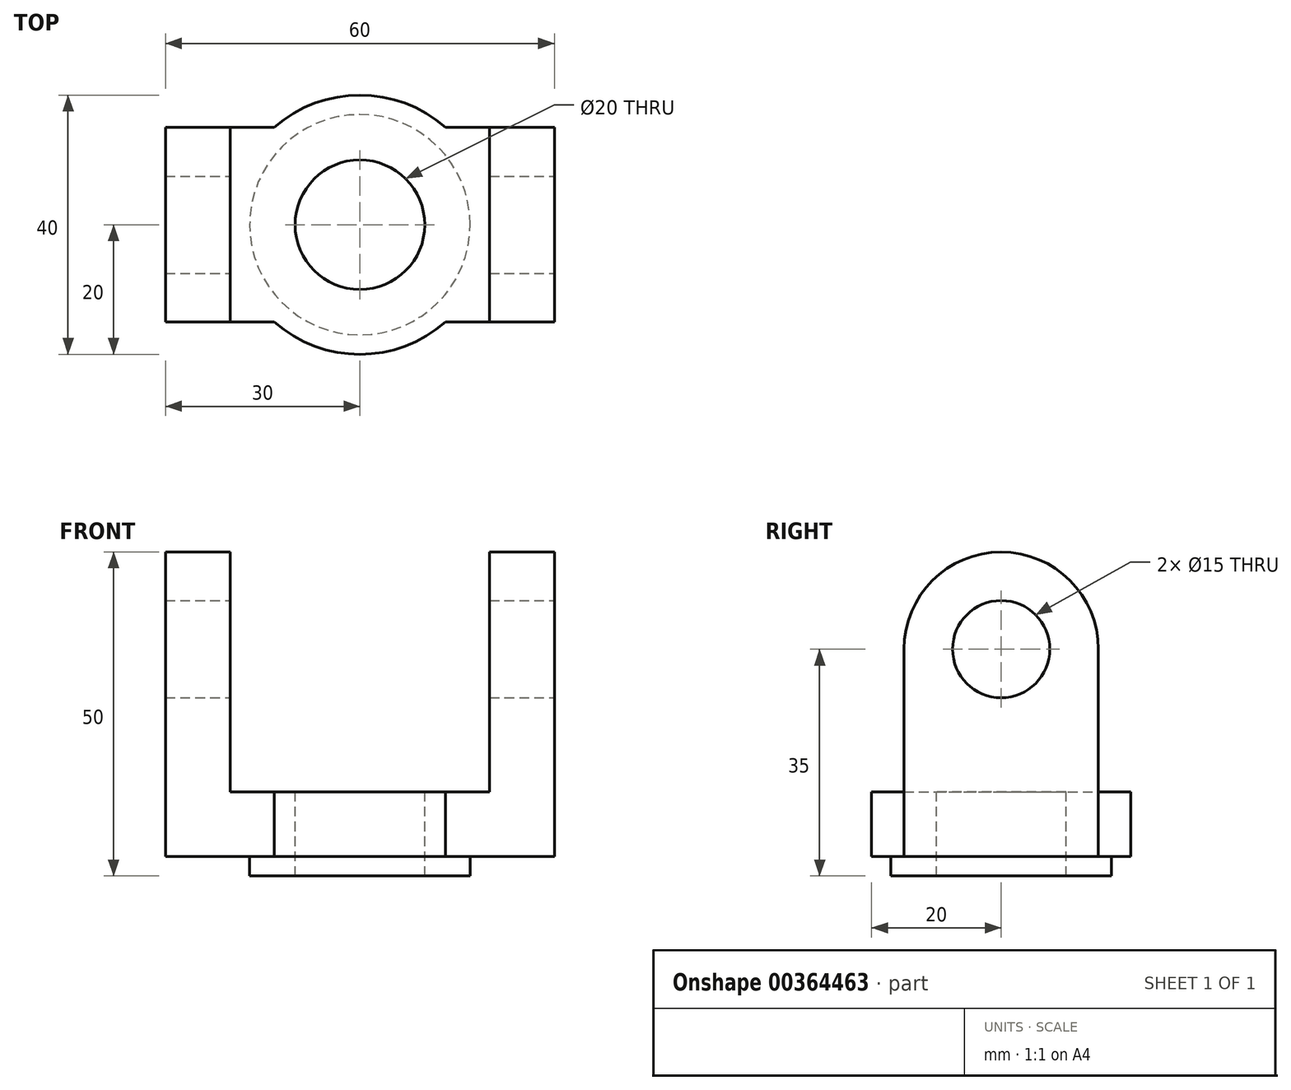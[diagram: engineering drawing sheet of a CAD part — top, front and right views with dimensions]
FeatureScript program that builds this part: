
annotation { "Feature Type Name" : "Feature", "Feature Type Description" : "" }
export const myFeature = defineFeature(function(context is Context, id is Id, definition is map)
    precondition{}
    {
        {
            var Q0;
            Q0=qCreatedBy(makeId("Top.planeOp"),FACE);
            var sketch = newSketch(context, id + "F0", { "sketchPlane" : qUnion([Q0])});
            skCircle(sketch, "E0", {"center": v(0, 0) * mm, "radius": 17 * mm});
            skSolve(sketch);
        }
        {
            var Q0;
            Q0 = qSketchRegion(id + "F0", true);
            extrude(context, id + "F1", {"entities" : qUnion([Q0]), "depth" : 3 * mm});
        }
        {
            var Q0;
            Q0=makeQuery(id+"F1.opExtrude","CAP_FACE",FACE,{"disambiguationData":[OSD([sQuery(id+"F0.wireOp",EDGE,"E0")])],"isStart":false});
            var sketch = newSketch(context, id + "F2", { "sketchPlane" : qUnion([Q0])});
            skCircle(sketch, "E1", {"center": v(0, 0) * mm, "radius": 20 * mm});
            skLineSegment(sketch, "E2.bottom", {"start": v(-30, -15) * mm, "end": v(30, -15) * mm});
            skLineSegment(sketch, "E2.top", {"start": v(-30, 15) * mm, "end": v(30, 15) * mm});
            skLineSegment(sketch, "E2.left", {"start": v(-30, -15) * mm, "end": v(-30, 15) * mm});
            skLineSegment(sketch, "E2.right", {"start": v(30, -15) * mm, "end": v(30, 15) * mm});
            skSolve(sketch);
        }
        {
            var Q0;
            Q0 = qSketchRegion(id + "F2", true);
            extrude(context, id + "F3", {"entities" : qUnion([Q0]), "operationType" : NewBodyOperationType.ADD, "depth" : 10 * mm});
        }
        {
            var Q0;
            Q0=makeQuery(id+"F3.opExtrude","CAP_FACE",FACE,{"disambiguationData":[OSD([sQuery(id+"F2.wireOp",EDGE,"E1"),sQuery(id+"F2.wireOp",EDGE,"E2.bottom"),sQuery(id+"F2.wireOp",EDGE,"E2.top"),sQuery(id+"F2.wireOp",EDGE,"E2.left"),sQuery(id+"F2.wireOp",EDGE,"E2.right")])],"isStart":false});
            var sketch = newSketch(context, id + "F4", { "sketchPlane" : qUnion([Q0])});
            skCircle(sketch, "E3", {"center": v(0, 0) * mm, "radius": 10 * mm});
            skSolve(sketch);
        }
        {
            var Q0;
            Q0 = qSketchRegion(id + "F4", true);
            extrude(context, id + "F5", {"entities" : qUnion([Q0]), "operationType" : NewBodyOperationType.REMOVE, "endBound" : BoundingType.THROUGH_ALL, "oppositeDirection" : true, "depth" : 25 * mm});
        }
        {
            var Q0;
            Q0=makeQuery(id+"F3.opExtrude","CAP_FACE",FACE,{"disambiguationData":[OSD([sQuery(id+"F2.wireOp",EDGE,"E1"),sQuery(id+"F2.wireOp",EDGE,"E2.bottom"),sQuery(id+"F2.wireOp",EDGE,"E2.top"),sQuery(id+"F2.wireOp",EDGE,"E2.left"),sQuery(id+"F2.wireOp",EDGE,"E2.right")])],"isStart":false});
            var sketch = newSketch(context, id + "F6", { "sketchPlane" : qUnion([Q0])});
            skLineSegment(sketch, "E4.bottom", {"start": v(-30, -15) * mm, "end": v(-20, -15) * mm});
            skLineSegment(sketch, "E4.top", {"start": v(-30, 15) * mm, "end": v(-20, 15) * mm});
            skLineSegment(sketch, "E4.left", {"start": v(-30, -15) * mm, "end": v(-30, 15) * mm});
            skLineSegment(sketch, "E4.right", {"start": v(-20, -15) * mm, "end": v(-20, 15) * mm});
            skLineSegment(sketch, "E5.bottom", {"start": v(30, -15) * mm, "end": v(20, -15) * mm});
            skLineSegment(sketch, "E5.top", {"start": v(30, 15) * mm, "end": v(20, 15) * mm});
            skLineSegment(sketch, "E5.left", {"start": v(30, -15) * mm, "end": v(30, 15) * mm});
            skLineSegment(sketch, "E5.right", {"start": v(20, -15) * mm, "end": v(20, 15) * mm});
            skSolve(sketch);
        }
        {
            var Q0;
            Q0 = qSketchRegion(id + "F6", true);
            extrude(context, id + "F7", {"entities" : qUnion([Q0]), "operationType" : NewBodyOperationType.ADD, "depth" : 40 * mm});
        }
        {
            var Q0;
            Q0=makeQuery(id+"F7.boolean.opBoolean","MERGE",FACE,{"derivedFrom":[makeQuery(id+"F3.opExtrude","SWEPT_FACE",FACE,{"disambiguationData":[OSD([sQuery(id+"F2.wireOp",EDGE,"E2.right")])]}),makeQuery(id+"F7.opExtrude","SWEPT_FACE",FACE,{"disambiguationData":[OSD([sQuery(id+"F6.wireOp",EDGE,"E5.left")])]})]});
            var sketch = newSketch(context, id + "F8", { "sketchPlane" : qUnion([Q0])});
            skCircle(sketch, "E6", {"center": v(0, 35) * mm, "radius": 7.5 * mm});
            skSolve(sketch);
        }
        {
            var Q0;
            Q0 = qSketchRegion(id + "F8", true);
            extrude(context, id + "F9", {"entities" : qUnion([Q0]), "operationType" : NewBodyOperationType.REMOVE, "endBound" : BoundingType.THROUGH_ALL, "oppositeDirection" : true, "depth" : 25 * mm});
        }
        {
            var Q0;
            Q0=makeQuery(id+"F7.boolean.opBoolean","MERGE",FACE,{"derivedFrom":[makeQuery(id+"F3.opExtrude","SWEPT_FACE",FACE,{"disambiguationData":[OSD([sQuery(id+"F2.wireOp",EDGE,"E2.right")])]}),makeQuery(id+"F7.opExtrude","SWEPT_FACE",FACE,{"disambiguationData":[OSD([sQuery(id+"F6.wireOp",EDGE,"E5.left")])]})]});
            var sketch = newSketch(context, id + "F10", { "sketchPlane" : qUnion([Q0])});
            skArc(sketch, "E7", {"start": v(15, 35) * mm, "mid": v(0, 50) * mm, "end": v(-15, 35) * mm});
            skLineSegment(sketch, "E8", {"start": v(-15, 35) * mm, "end": v(-15, 53) * mm});
            skLineSegment(sketch, "E9", {"start": v(-15, 53) * mm, "end": v(15, 53) * mm});
            skLineSegment(sketch, "E10", {"start": v(15, 53) * mm, "end": v(15, 35) * mm});
            skSolve(sketch);
        }
        {
            var Q0;
            Q0 = qSketchRegion(id + "F10", true);
            extrude(context, id + "F11", {"entities" : qUnion([Q0]), "operationType" : NewBodyOperationType.REMOVE, "endBound" : BoundingType.THROUGH_ALL, "oppositeDirection" : true, "depth" : 25 * mm});
        }
    });
